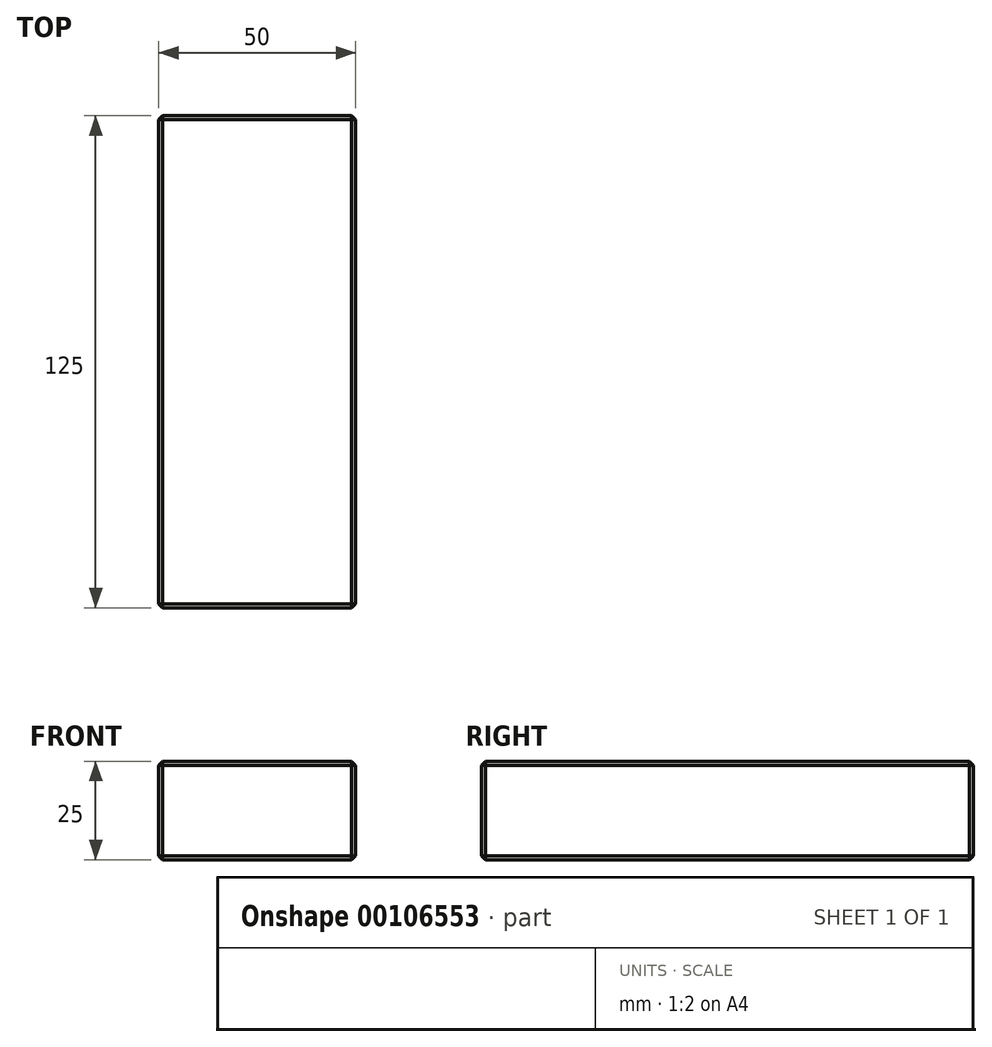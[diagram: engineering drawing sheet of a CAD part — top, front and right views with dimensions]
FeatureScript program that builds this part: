
annotation { "Feature Type Name" : "Feature", "Feature Type Description" : "" }
export const myFeature = defineFeature(function(context is Context, id is Id, definition is map)
    precondition{}
    {
        {
            var Q0;
            Q0=qCreatedBy(makeId("Front.planeOp"),FACE);
            var sketch = newSketch(context, id + "F0", { "sketchPlane" : qUnion([Q0])});
            skLineSegment(sketch, "E0.bottom", {"start": v(25, -12.5) * mm, "end": v(-25, -12.5) * mm});
            skLineSegment(sketch, "E0.top", {"start": v(25, 12.5) * mm, "end": v(-25, 12.5) * mm});
            skLineSegment(sketch, "E0.left", {"start": v(25, -12.5) * mm, "end": v(25, 12.5) * mm});
            skLineSegment(sketch, "E0.right", {"start": v(-25, -12.5) * mm, "end": v(-25, 12.5) * mm});
            skPoint(sketch, "E0.middle", {"position": v(0, 0) * mm});
            skSolve(sketch);
        }
        {
            var Q0;
            Q0=makeQuery(id+"F0.imprint","IMPRINT",FACE,{"disambiguationData":[TD([[makeQuery(id+"F0.imprint","IMPRINT",EDGE,{"derivedFrom":sQuery(id+"F0.wireOp",EDGE,"E0.bottom")}),-1.0]])]});
            extrude(context, id + "F1", {"entities" : qUnion([Q0]), "endBound" : BoundingType.SYMMETRIC, "depth" : 125 * mm});
        }
        {
            var Q0;
            Q0=makeQuery(id+"F1.opExtrude","SWEPT_EDGE",EDGE,{"disambiguationData":[OSD([sQuery(id+"F0.wireOp",EDGE,"E0.top"),sQuery(id+"F0.wireOp",EDGE,"E0.left")])]});
            var Q1;
            Q1=makeQuery(id+"F1.opExtrude","CAP_EDGE",EDGE,{"disambiguationData":[OSD([sQuery(id+"F0.wireOp",EDGE,"E0.left")])],"isStart":false});
            var Q2;
            Q2=makeQuery(id+"F1.opExtrude","CAP_EDGE",EDGE,{"disambiguationData":[OSD([sQuery(id+"F0.wireOp",EDGE,"E0.top")])],"isStart":false});
            var Q3;
            Q3=makeQuery(id+"F1.opExtrude","CAP_EDGE",EDGE,{"disambiguationData":[OSD([sQuery(id+"F0.wireOp",EDGE,"E0.right")])],"isStart":false});
            var Q4;
            Q4=makeQuery(id+"F1.opExtrude","CAP_EDGE",EDGE,{"disambiguationData":[OSD([sQuery(id+"F0.wireOp",EDGE,"E0.bottom")])],"isStart":false});
            var Q5;
            Q5=makeQuery(id+"F1.opExtrude","SWEPT_EDGE",EDGE,{"disambiguationData":[OSD([sQuery(id+"F0.wireOp",EDGE,"E0.bottom"),sQuery(id+"F0.wireOp",EDGE,"E0.left")])]});
            var Q6;
            Q6=makeQuery(id+"F1.opExtrude","SWEPT_EDGE",EDGE,{"disambiguationData":[OSD([sQuery(id+"F0.wireOp",EDGE,"E0.top"),sQuery(id+"F0.wireOp",EDGE,"E0.right")])]});
            var Q7;
            Q7=makeQuery(id+"F1.opExtrude","SWEPT_EDGE",EDGE,{"disambiguationData":[OSD([sQuery(id+"F0.wireOp",EDGE,"E0.bottom"),sQuery(id+"F0.wireOp",EDGE,"E0.right")])]});
            var Q8;
            Q8=makeQuery(id+"F1.opExtrude","CAP_EDGE",EDGE,{"disambiguationData":[OSD([sQuery(id+"F0.wireOp",EDGE,"E0.bottom")])],"isStart":true});
            var Q9;
            Q9=makeQuery(id+"F1.opExtrude","CAP_EDGE",EDGE,{"disambiguationData":[OSD([sQuery(id+"F0.wireOp",EDGE,"E0.right")])],"isStart":true});
            var Q10;
            Q10=makeQuery(id+"F1.opExtrude","CAP_EDGE",EDGE,{"disambiguationData":[OSD([sQuery(id+"F0.wireOp",EDGE,"E0.top")])],"isStart":true});
            var Q11;
            Q11=makeQuery(id+"F1.opExtrude","CAP_EDGE",EDGE,{"disambiguationData":[OSD([sQuery(id+"F0.wireOp",EDGE,"E0.left")])],"isStart":true});
            chamfer(context, id + "F2", {"entities" : qUnion([Q0, Q1, Q2, Q3, Q4, Q5, Q6, Q7, Q8, Q9, Q10, Q11]), "width" : 1 * mm, "tangentPropagation" : true});
        }
    });
